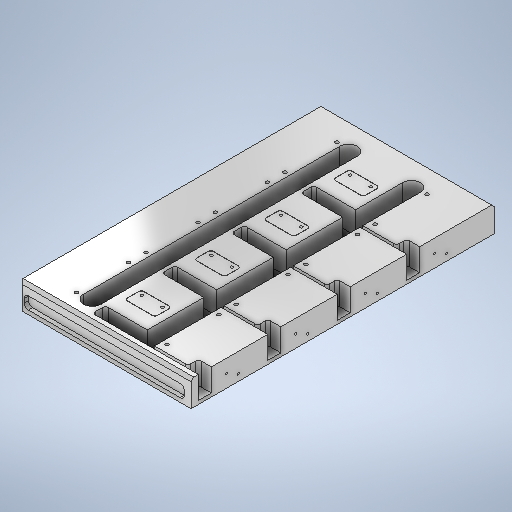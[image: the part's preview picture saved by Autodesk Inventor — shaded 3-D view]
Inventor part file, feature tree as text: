
AUTODESK INVENTOR PART (.ipt)
format: ipt  version: 2025 (Build 290162000, 162)  size: 676,864 bytes
history: native  units: in
note: dims shown in document units (in); Inventor stores cm internally (conversion verified against a paired STEP export)
features: sketch x10, extrude x6, hole x4, chamfer x2
ambient origin geometry x8: Origin, YZ Plane, XZ Plane, XY Plane, X Axis, Y Axis, Z Axis, Center Point
bodies: Solid1 (feature_tree)
feature tree (22):
  extrude  "Extrusion1"  Depth=8.7402in
  extrude  "Extrusion4"  Depth=0.3543in
  extrude  "Extrusion5"  Depth=0.1969in
  chamfer  "Chamfer3"  Distance=0.1181in
  hole  "Hole6"  [1 undecoded]
  chamfer  "Chamfer4"  Distance=0.1181in
  hole  "Hole8"  [1 undecoded]
  extrude  "Extrusion13"  Depth=0.4593in
  hole  "Hole5"  [1 undecoded]
  extrude  "Extrusion12"  Depth=0.5in
  extrude  "Extrusion11"  Depth=1.811in
  hole  "Hole9"  [1 undecoded]
  sketch  "Sketch Rectangular Pattern2"  dims[d0=5.0in d1=8.7402in]
  sketch  "Sketch16"  dims[d89=0.1181in d91=0.1181in d92=0.0in]
  sketch  "Sketch17"  dims[d93=0.1969in d94=0.1969in]
  sketch  "Sketch Rectangular Pattern9"  dims[d2=0.75in d3=0.0in d77=0.3543in]
  sketch  "Sketch Rectangular Pattern11"  dims[d78=0.1969in d79=0.1969in]
  sketch  "Sketch18"  dims[d96=0.561in d97=0.4593in]
  sketch  "Sketch19"  dims[d99=0.156in d100=0.38in d101=0.5in d102=0.6102in d103=0.5635in d104=1.0in d105=0.8108in d113=0.0787in d114=0.0787in d115=45.0deg]
  sketch  "Sketch Rectangular Pattern12"  dims[d80=0.1181in d81=0.1181in d82=0.0in]
  sketch  "Sketch20"  dims[d127=0.4593in d128=0.4593in d129=1.811in d130=1.378in d131=0.689in d132=0.9055in d133=1.2992in d134=0.748in d135=1.4961in d136=1.2992in d137=0.0968in d138=0.2362in d139=0.119in d140=0.0787in d141=0.5635in d142=0.315in d143=0.8108in d144=1.5748in d146=2.0in d147=0.3937in d149=0.3937in d151=0.1575in d152=0.0787in d153=45.0deg d154=2.5in d155=5.0in d217=0.5906in d226=0.0787in d227=0.2726in d228=0.1575in d229=0.0787in d230=90.0deg d231=0.315in d232=0.8108in d234=0.374in d235=0.374in d236=0.374in d237=1.0236in d238=0.5512in d239=2.0in d247=0.6496in d248=0.0in d249=0.2953in d251=1.4961in d252=0.878in d253=2.0in d254=1.5748in d256=2.0in d257=0.3937in d259=0.3937in d262=0.0787in d263=0.2913in d271=0.0787in d272=1.5748in d274=2.0in d275=0.3937in d277=0.3937in d279=0.6496in d280=0.0in d281=0.1181in d282=0.3543in d283=0.8661in d284=0.0787in d285=2.0in d286=1.5748in d288=2.0in d289=0.3937in d291=0.3937in d293=0.0079in d294=0.0in d295=0.432in d296=0.775in d297=0.364in d298=0.192in d299=2.0in d300=1.5748in d302=2.0in d303=0.3937in d305=0.3937in d307=0.0617in d308=0.1575in d309=0.5in d310=0.6102in d311=90.0deg d312=0.248in d313=0.8108in d156=0.0148in d157=0.5635in d158=0.0295in d159=0.8108in d160=0.0025in d161=0.0295in d162=0.0148in]
  sketch  "Sketch Rectangular Pattern13"  dims[d83=0.1181in d84=0.3543in d88=0.1181in]
note: 4 required parameter values undecoded (feature->parameter linkage not recoverable at this tier; creation-order binding heuristic only, values carry confidence <= 0.55)
